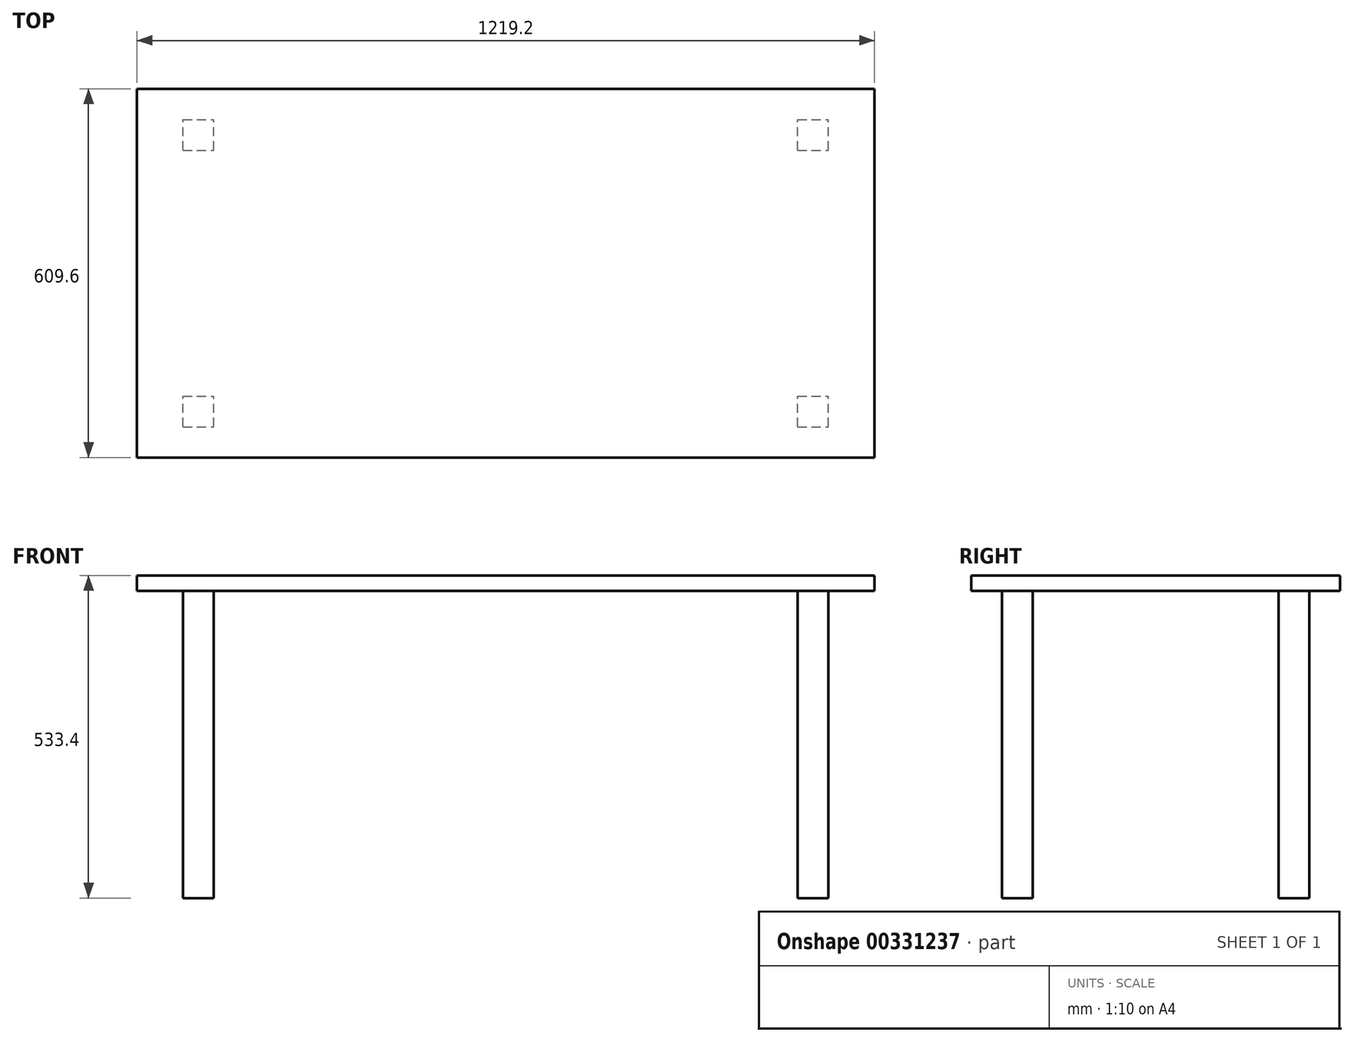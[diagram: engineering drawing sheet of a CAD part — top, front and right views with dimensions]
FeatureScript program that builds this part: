
annotation { "Feature Type Name" : "Feature", "Feature Type Description" : "" }
export const myFeature = defineFeature(function(context is Context, id is Id, definition is map)
    precondition{}
    {
        {
            var Q0;
            Q0=qCreatedBy(makeId("Top.planeOp"),FACE);
            var sketch = newSketch(context, id + "F0", { "sketchPlane" : qUnion([Q0])});
            skLineSegment(sketch, "E0.bottom", {"start": v(-609.6, 304.8) * mm, "end": v(609.6, 304.8) * mm});
            skLineSegment(sketch, "E0.top", {"start": v(-609.6, -304.8) * mm, "end": v(609.6, -304.8) * mm});
            skLineSegment(sketch, "E0.left", {"start": v(-609.6, 304.8) * mm, "end": v(-609.6, -304.8) * mm});
            skLineSegment(sketch, "E0.right", {"start": v(609.6, 304.8) * mm, "end": v(609.6, -304.8) * mm});
            skPoint(sketch, "E0.middle", {"position": v(0, 0) * mm});
            skSolve(sketch);
        }
        {
            var Q0;
            Q0=makeQuery(id+"F0.imprint","IMPRINT",FACE,{"disambiguationData":[TD([[makeQuery(id+"F0.imprint","IMPRINT",EDGE,{"derivedFrom":sQuery(id+"F0.wireOp",EDGE,"E0.bottom")}),-1.0]])]});
            extrude(context, id + "F1", {"entities" : qUnion([Q0]), "depth" : 25.4 * mm});
        }
        {
            var Q0;
            Q0=makeQuery(id+"F1.opExtrude","CAP_FACE",FACE,{"disambiguationData":[OSD([sQuery(id+"F0.wireOp",EDGE,"E0.bottom"),sQuery(id+"F0.wireOp",EDGE,"E0.top"),sQuery(id+"F0.wireOp",EDGE,"E0.left"),sQuery(id+"F0.wireOp",EDGE,"E0.right")])],"isStart":true});
            var sketch = newSketch(context, id + "F2", { "sketchPlane" : qUnion([Q0])});
            skLineSegment(sketch, "E1.bottom", {"start": v(-533.4, 254) * mm, "end": v(-482.6, 254) * mm});
            skLineSegment(sketch, "E1.top", {"start": v(-533.4, 203.2) * mm, "end": v(-482.6, 203.2) * mm});
            skLineSegment(sketch, "E1.left", {"start": v(-533.4, 254) * mm, "end": v(-533.4, 203.2) * mm});
            skLineSegment(sketch, "E1.right", {"start": v(-482.6, 254) * mm, "end": v(-482.6, 203.2) * mm});
            skPoint(sketch, "E1.middle", {"position": v(-508, 228.6) * mm});
            skLineSegment(sketch, "E2.bottom", {"start": v(-533.4, -203.2) * mm, "end": v(-482.6, -203.2) * mm});
            skLineSegment(sketch, "E2.top", {"start": v(-533.4, -254) * mm, "end": v(-482.6, -254) * mm});
            skLineSegment(sketch, "E2.left", {"start": v(-533.4, -203.2) * mm, "end": v(-533.4, -254) * mm});
            skLineSegment(sketch, "E2.right", {"start": v(-482.6, -203.2) * mm, "end": v(-482.6, -254) * mm});
            skPoint(sketch, "E2.middle", {"position": v(-508, -228.6) * mm});
            skLineSegment(sketch, "E3.bottom", {"start": v(482.6, 254) * mm, "end": v(533.4, 254) * mm});
            skLineSegment(sketch, "E3.top", {"start": v(482.6, 203.2) * mm, "end": v(533.4, 203.2) * mm});
            skLineSegment(sketch, "E3.left", {"start": v(482.6, 254) * mm, "end": v(482.6, 203.2) * mm});
            skLineSegment(sketch, "E3.right", {"start": v(533.4, 254) * mm, "end": v(533.4, 203.2) * mm});
            skPoint(sketch, "E3.middle", {"position": v(508, 228.6) * mm});
            skLineSegment(sketch, "E4.bottom", {"start": v(482.6, -203.2) * mm, "end": v(533.4, -203.2) * mm});
            skLineSegment(sketch, "E4.top", {"start": v(482.6, -254) * mm, "end": v(533.4, -254) * mm});
            skLineSegment(sketch, "E4.left", {"start": v(482.6, -203.2) * mm, "end": v(482.6, -254) * mm});
            skLineSegment(sketch, "E4.right", {"start": v(533.4, -203.2) * mm, "end": v(533.4, -254) * mm});
            skPoint(sketch, "E4.middle", {"position": v(508, -228.6) * mm});
            skSolve(sketch);
        }
        {
            var Q0;
            Q0 = qSketchRegion(id + "F2", true);
            extrude(context, id + "F3", {"entities" : qUnion([Q0]), "operationType" : NewBodyOperationType.ADD, "depth" : 508 * mm});
        }
    });
